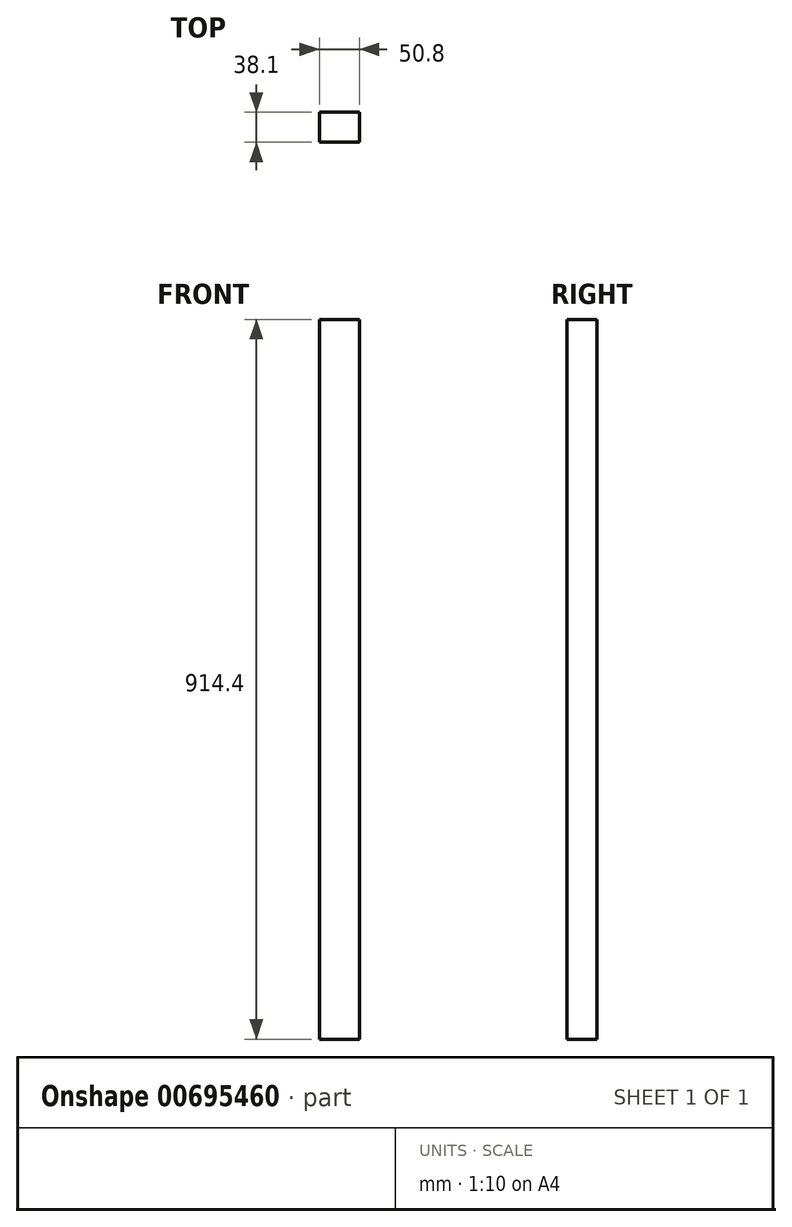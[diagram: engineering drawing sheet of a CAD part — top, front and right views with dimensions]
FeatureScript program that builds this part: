
annotation { "Feature Type Name" : "Feature", "Feature Type Description" : "" }
export const myFeature = defineFeature(function(context is Context, id is Id, definition is map)
    precondition{}
    {
        {
            var Q0;
            Q0=qCreatedBy(makeId("Front.planeOp"),FACE);
            var sketch = newSketch(context, id + "F0", { "sketchPlane" : qUnion([Q0])});
            skLineSegment(sketch, "E0.bottom", {"start": v(-25.4, 457.2) * mm, "end": v(25.4, 457.2) * mm});
            skLineSegment(sketch, "E0.top", {"start": v(-25.4, -457.2) * mm, "end": v(25.4, -457.2) * mm});
            skLineSegment(sketch, "E0.left", {"start": v(-25.4, 457.2) * mm, "end": v(-25.4, -457.2) * mm});
            skLineSegment(sketch, "E0.right", {"start": v(25.4, 457.2) * mm, "end": v(25.4, -457.2) * mm});
            skPoint(sketch, "E0.middle", {"position": v(0, 0) * mm});
            skSolve(sketch);
        }
        {
            var Q0;
            Q0=makeQuery(id+"F0.imprint","IMPRINT",FACE,{"disambiguationData":[TD([[makeQuery(id+"F0.imprint","IMPRINT",EDGE,{"derivedFrom":sQuery(id+"F0.wireOp",EDGE,"E0.bottom")}),-1.0]])]});
            extrude(context, id + "F1", {"entities" : qUnion([Q0]), "depth" : 38.1 * mm, "offsetDistance" : 25.4 * mm, "symmetric" : true});
        }
    });
